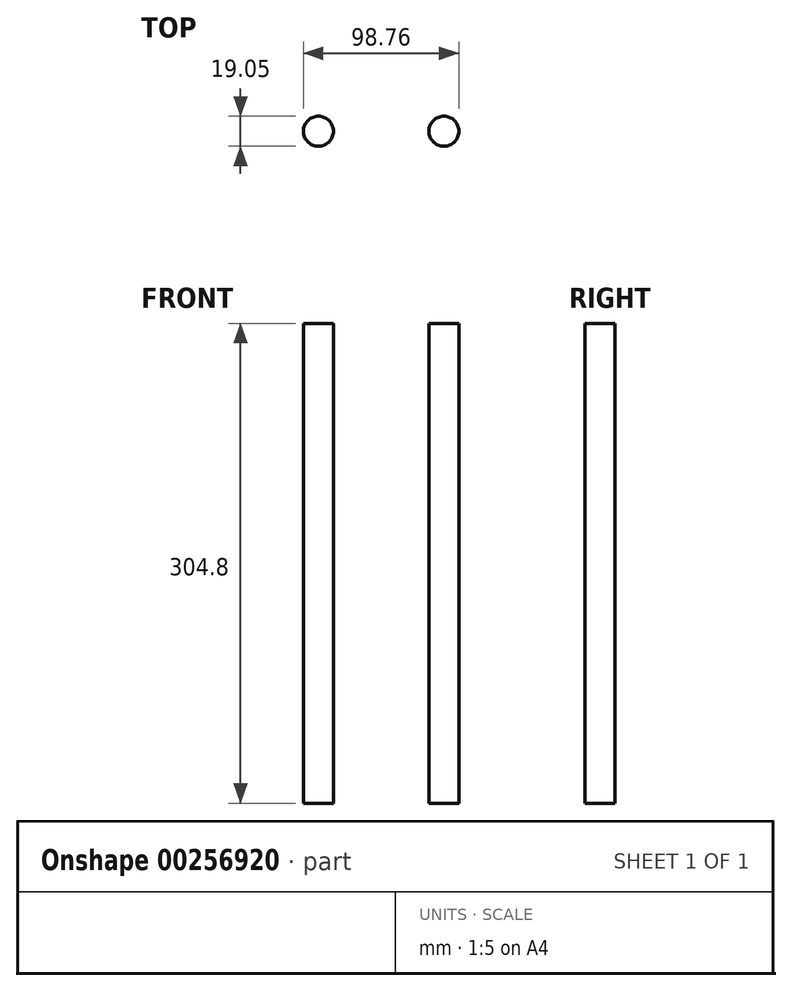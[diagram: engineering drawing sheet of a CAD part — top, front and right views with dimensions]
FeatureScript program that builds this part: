
annotation { "Feature Type Name" : "Feature", "Feature Type Description" : "" }
export const myFeature = defineFeature(function(context is Context, id is Id, definition is map)
    precondition{}
    {
        {
            var Q0;
            Q0=qCreatedBy(makeId("Top.planeOp"),FACE);
            var sketch = newSketch(context, id + "F0", { "sketchPlane" : qUnion([Q0])});
            skCircle(sketch, "E0", {"center": v(-39.85, 15.33) * mm, "radius": 9.53 * mm});
            skCircle(sketch, "E1.MirrorC", {"center": v(39.85, 15.33) * mm, "radius": 9.53 * mm});
            skSolve(sketch);
        }
        {
            var Q0;
            Q0 = qSketchRegion(id + "F0", true);
            extrude(context, id + "F1", {"entities" : qUnion([Q0]), "depth" : 304.8 * mm});
        }
    });
